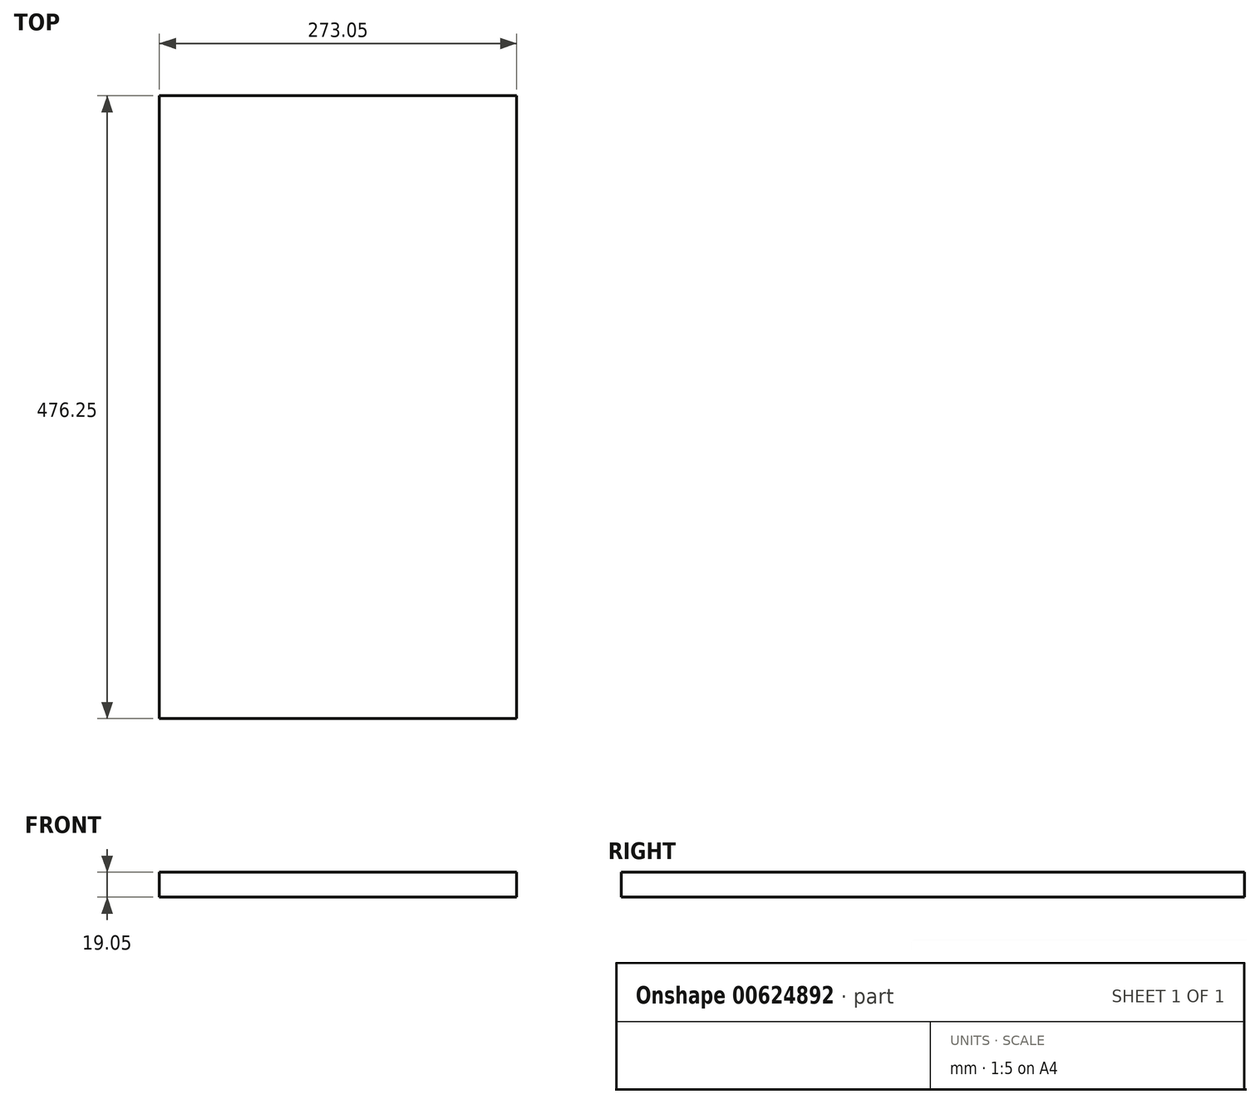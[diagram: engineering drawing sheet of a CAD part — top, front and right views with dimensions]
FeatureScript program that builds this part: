
annotation { "Feature Type Name" : "Feature", "Feature Type Description" : "" }
export const myFeature = defineFeature(function(context is Context, id is Id, definition is map)
    precondition{}
    {
        {
            var Q0;
            Q0=qCreatedBy(makeId("Top.planeOp"),FACE);
            var sketch = newSketch(context, id + "F0", { "sketchPlane" : qUnion([Q0])});
            skLineSegment(sketch, "E0.bottom", {"start": v(0, 0) * mm, "end": v(-273.05, 0) * mm});
            skLineSegment(sketch, "E0.top", {"start": v(0, -476.25) * mm, "end": v(-273.05, -476.25) * mm});
            skLineSegment(sketch, "E0.left", {"start": v(0, 0) * mm, "end": v(0, -476.25) * mm});
            skLineSegment(sketch, "E0.right", {"start": v(-273.05, 0) * mm, "end": v(-273.05, -476.25) * mm});
            skLineSegment(sketch, "E1", {"start": v(-257.18, -476.25) * mm, "end": v(-257.18, 0) * mm});
            skLineSegment(sketch, "E2", {"start": v(-15.88, 0) * mm, "end": v(-15.87, -476.25) * mm});
            skLineSegment(sketch, "E3", {"start": v(-273.05, -460.38) * mm, "end": v(0, -460.38) * mm});
            skLineSegment(sketch, "E4", {"start": v(-273.05, -15.88) * mm, "end": v(0, -15.87) * mm});
            skSolve(sketch);
        }
        {
            var Q0;
            {var subQ0=sQuery(id+"F0.wireOp",EDGE,"E3");var subQ1=sQuery(id+"F0.wireOp",EDGE,"E1");var subQ2=makeQuery(id+"F0.imprint","INTERSECT",VERTEX,{"derivedFrom":[subQ1,subQ0]});Q0=makeQuery(id+"F0.imprint","IMPRINT",FACE,{"disambiguationData":[TD([[makeQuery(id+"F0.imprint","IMPRINT",EDGE,{"disambiguationData":[TD([[subQ2,-1.0]])],"derivedFrom":subQ1}),-1.0]])]});}
            var Q1;
            {var subQ0=sQuery(id+"F0.wireOp",EDGE,"E1");var subQ1=sQuery(id+"F0.wireOp",EDGE,"E0.bottom");var subQ2=makeQuery(id+"F0.imprint","INTERSECT",VERTEX,{"derivedFrom":[subQ1,subQ0]});Q1=makeQuery(id+"F0.imprint","IMPRINT",FACE,{"disambiguationData":[TD([[makeQuery(id+"F0.imprint","IMPRINT",EDGE,{"disambiguationData":[TD([[subQ2,1.0]])],"derivedFrom":subQ1}),1.0]])]});}
            var Q2;
            {var subQ0=sQuery(id+"F0.wireOp",EDGE,"E3");var subQ1=sQuery(id+"F0.wireOp",EDGE,"E0.right");var subQ2=makeQuery(id+"F0.imprint","INTERSECT",VERTEX,{"derivedFrom":[subQ1,subQ0]});Q2=makeQuery(id+"F0.imprint","IMPRINT",FACE,{"disambiguationData":[TD([[makeQuery(id+"F0.imprint","IMPRINT",EDGE,{"disambiguationData":[TD([[subQ2,1.0]])],"derivedFrom":subQ1}),1.0]])]});}
            var Q3;
            {var subQ0=sQuery(id+"F0.wireOp",EDGE,"E1");var subQ1=sQuery(id+"F0.wireOp",EDGE,"E0.top");var subQ2=makeQuery(id+"F0.imprint","INTERSECT",VERTEX,{"derivedFrom":[subQ1,subQ0]});Q3=makeQuery(id+"F0.imprint","IMPRINT",FACE,{"disambiguationData":[TD([[makeQuery(id+"F0.imprint","IMPRINT",EDGE,{"disambiguationData":[TD([[subQ2,1.0]])],"derivedFrom":subQ1}),-1.0]])]});}
            var Q4;
            {var subQ0=sQuery(id+"F0.wireOp",EDGE,"E3");var subQ1=sQuery(id+"F0.wireOp",EDGE,"E0.left");var subQ2=makeQuery(id+"F0.imprint","INTERSECT",VERTEX,{"derivedFrom":[subQ1,subQ0]});Q4=makeQuery(id+"F0.imprint","IMPRINT",FACE,{"disambiguationData":[TD([[makeQuery(id+"F0.imprint","IMPRINT",EDGE,{"disambiguationData":[TD([[subQ2,1.0]])],"derivedFrom":subQ1}),-1.0]])]});}
            var Q5;
            {var subQ0=sQuery(id+"F0.wireOp",EDGE,"E0.right");var subQ1=sQuery(id+"F0.wireOp",EDGE,"E0.top");var subQ2=makeQuery(id+"F0.imprint","INTERSECT",VERTEX,{"derivedFrom":[subQ1,subQ0]});Q5=makeQuery(id+"F0.imprint","IMPRINT",FACE,{"disambiguationData":[TD([[makeQuery(id+"F0.imprint","IMPRINT",EDGE,{"disambiguationData":[TD([[subQ2,1.0]])],"derivedFrom":subQ1}),-1.0]])]});}
            var Q6;
            {var subQ0=sQuery(id+"F0.wireOp",EDGE,"E0.left");var subQ1=sQuery(id+"F0.wireOp",EDGE,"E0.top");var subQ2=makeQuery(id+"F0.imprint","INTERSECT",VERTEX,{"derivedFrom":[subQ1,subQ0]});Q6=makeQuery(id+"F0.imprint","IMPRINT",FACE,{"disambiguationData":[TD([[makeQuery(id+"F0.imprint","IMPRINT",EDGE,{"disambiguationData":[TD([[subQ2,-1.0]])],"derivedFrom":subQ1}),-1.0]])]});}
            var Q7;
            {var subQ0=sQuery(id+"F0.wireOp",EDGE,"E0.left");var subQ1=sQuery(id+"F0.wireOp",EDGE,"E0.bottom");var subQ2=makeQuery(id+"F0.imprint","INTERSECT",VERTEX,{"derivedFrom":[subQ1,subQ0]});Q7=makeQuery(id+"F0.imprint","IMPRINT",FACE,{"disambiguationData":[TD([[makeQuery(id+"F0.imprint","IMPRINT",EDGE,{"disambiguationData":[TD([[subQ2,-1.0]])],"derivedFrom":subQ1}),1.0]])]});}
            var Q8;
            {var subQ0=sQuery(id+"F0.wireOp",EDGE,"E0.right");var subQ1=sQuery(id+"F0.wireOp",EDGE,"E0.bottom");var subQ2=makeQuery(id+"F0.imprint","INTERSECT",VERTEX,{"derivedFrom":[subQ1,subQ0]});Q8=makeQuery(id+"F0.imprint","IMPRINT",FACE,{"disambiguationData":[TD([[makeQuery(id+"F0.imprint","IMPRINT",EDGE,{"disambiguationData":[TD([[subQ2,1.0]])],"derivedFrom":subQ1}),1.0]])]});}
            extrude(context, id + "F1", {"entities" : qUnion([Q0, Q1, Q2, Q3, Q4, Q5, Q6, Q7, Q8]), "depth" : 19.05 * mm, "offsetDistance" : 25.4 * mm});
        }
    });
